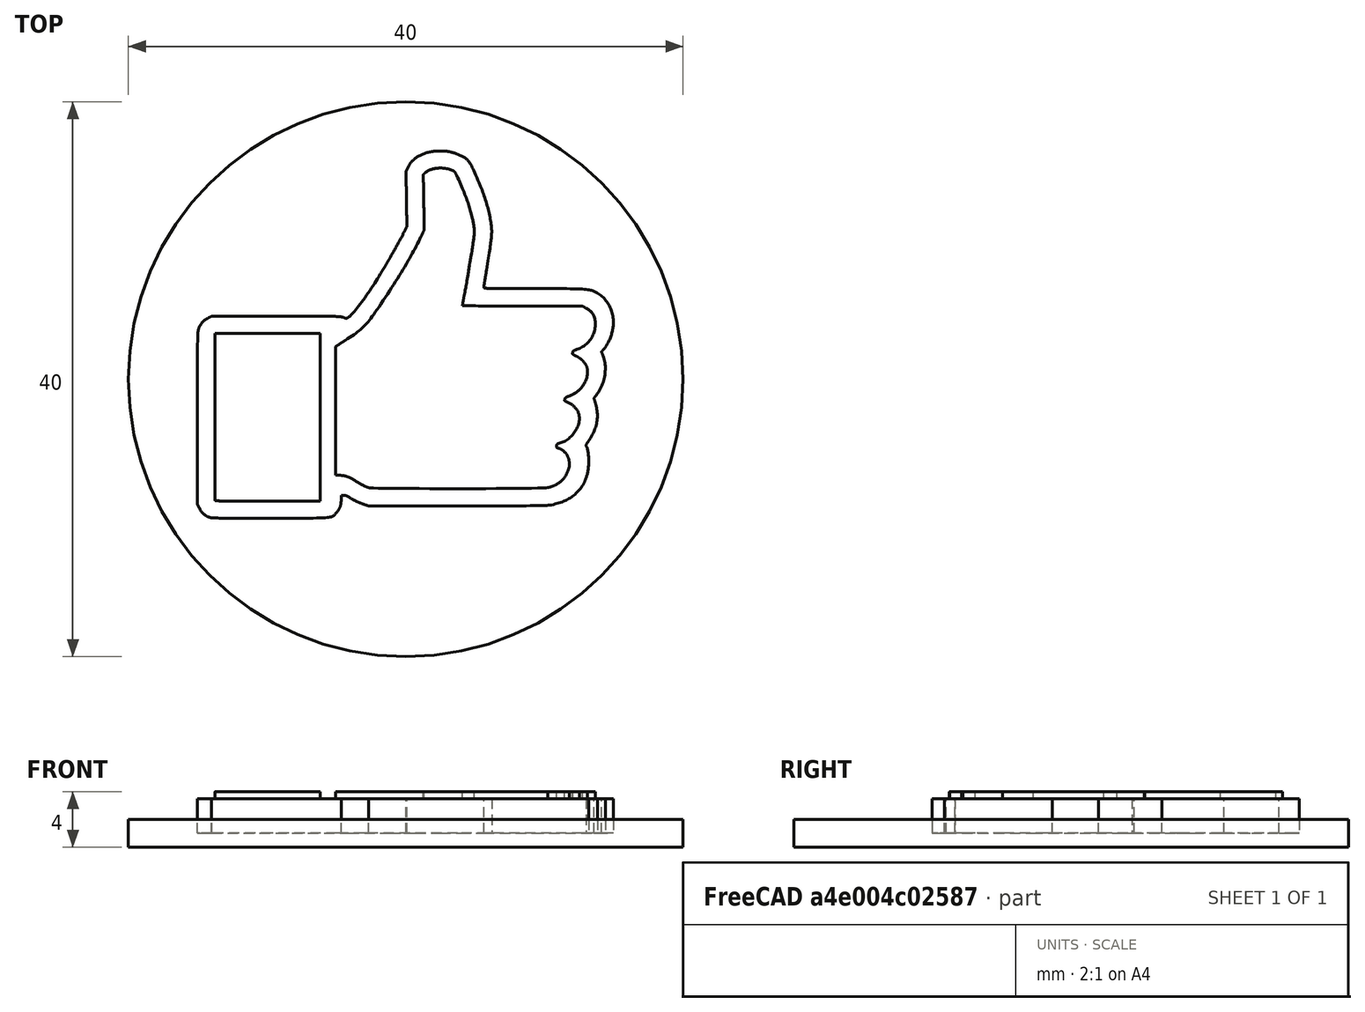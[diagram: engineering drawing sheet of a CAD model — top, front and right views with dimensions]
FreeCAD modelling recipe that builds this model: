
FCSTD DOCUMENT  (FreeCAD 0.17R13217 (Git))
Label: 10-like
License: All rights reserved
LicenseURL: http://en.wikipedia.org/wiki/All_rights_reserved
objects: Part::Feature×4, Part::Extrusion×3, Part::MultiFuse×1, Part::Cylinder×1
note: 9 computed .brp shape members not serialized (recipe doc carries the construction recipe); baked Part::Feature solids carry a one-line shape summary decoded from their .brp

FEATURE [Part::Feature] Wire
  shape: bbox 18.8 x 23.2 x 2e-07 mm, 0 faces, 0 solids (baked)
FEATURE [Part::Extrusion] Extrude
  Base = -> Wire
  Dir = (0,0,1)
  DirMode = 2
  FaceMakerClass = Part::FaceMakerBullseye
  LengthFwd = 3
  LengthRev = 0
  Solid = true
  Symmetric = false
FEATURE [Part::Feature] Wire001
  shape: bbox 30 x 26.52 x 2e-07 mm, 0 faces, 0 solids (baked)
FEATURE [Part::Feature] Wire002
  shape: bbox 18.8 x 23.2 x 2e-07 mm, 0 faces, 0 solids (baked)
FEATURE [Part::Feature] Wire003
  shape: bbox 7.591 x 12.1 x 2e-07 mm, 0 faces, 0 solids (baked)
FEATURE [Part::Extrusion] Extrude001
  Base = -> Wire001
  Dir = (0,0,-1)
  DirMode = 2
  FaceMakerClass = Part::FaceMakerBullseye
  LengthFwd = 2.5
  LengthRev = 0
  Reversed = true
  Solid = true
  Symmetric = false
FEATURE [Part::Extrusion] Extrude002
  Base = -> Wire003
  Dir = (0,0,1)
  DirMode = 2
  FaceMakerClass = Part::FaceMakerBullseye
  LengthFwd = 3
  LengthRev = 0
  Solid = true
  Symmetric = false
FEATURE [Part::MultiFuse] Fusion
  Placement = pos=(-15.0207,16.4598,1) rot=(0,0,1;0rad)
  Refine = true
  Shapes = -> [Extrude,Extrude001,Extrude002]
FEATURE [Part::Cylinder] Cylinder  label="Cilindro"
  Angle = 360
  AttacherType = Attacher::AttachEngine3D
  Height = 2
  Radius = 20
